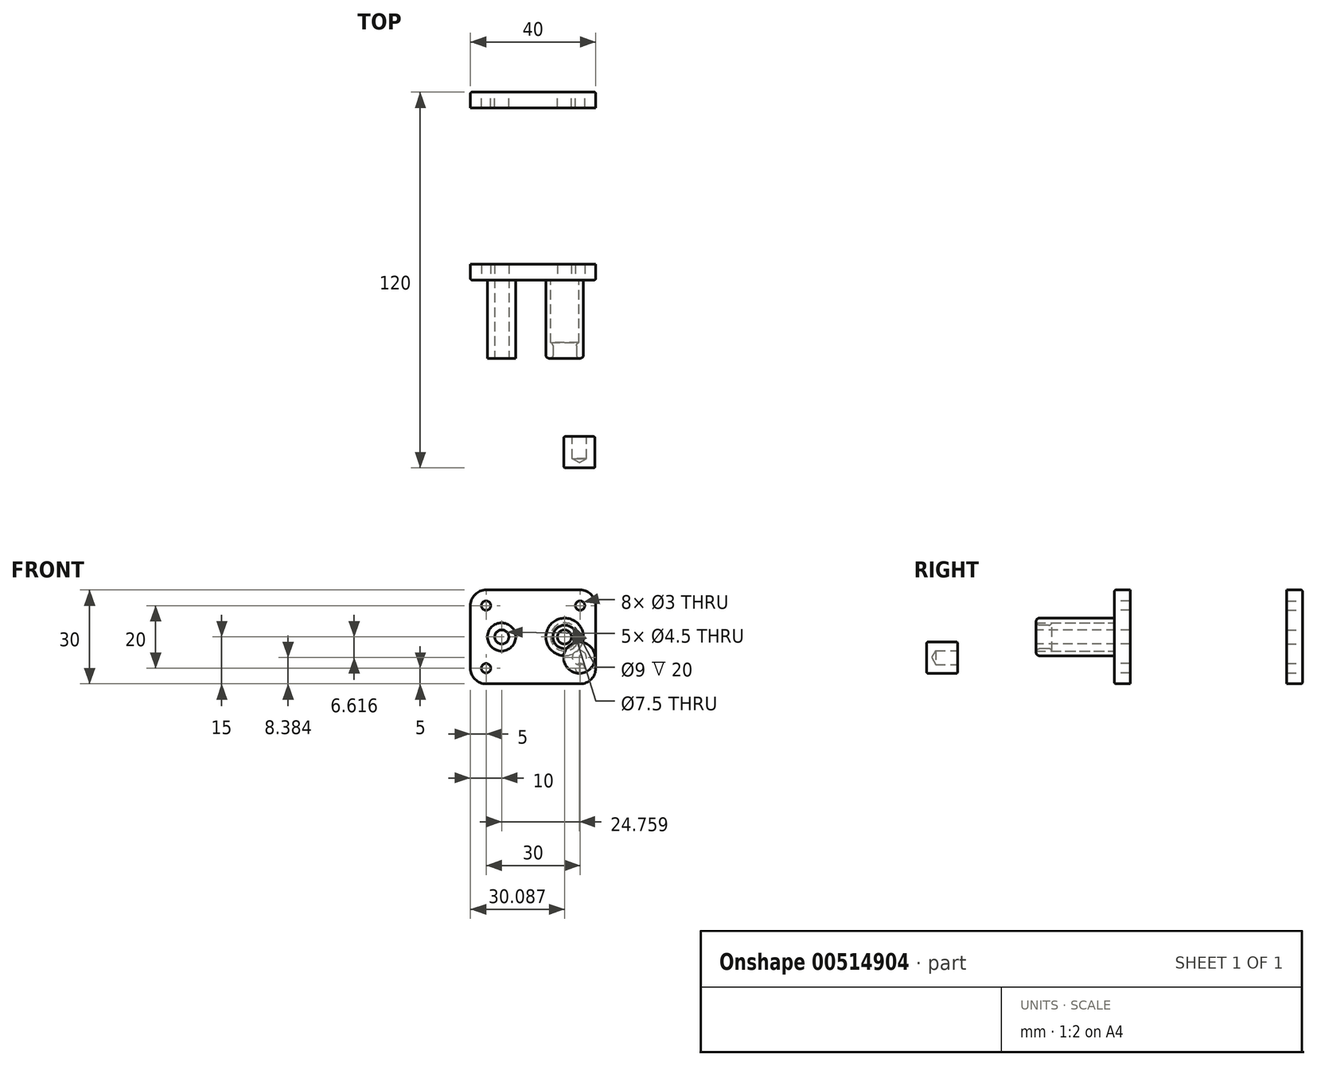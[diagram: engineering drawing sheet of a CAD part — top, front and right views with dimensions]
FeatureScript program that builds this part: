
annotation { "Feature Type Name" : "Feature", "Feature Type Description" : "" }
export const myFeature = defineFeature(function(context is Context, id is Id, definition is map)
    precondition{}
    {
        {
            var Q0;
            Q0=qCreatedBy(makeId("Front.planeOp"),FACE);
            var sketch = newSketch(context, id + "F0", { "sketchPlane" : qUnion([Q0])});
            skLineSegment(sketch, "E0.bottom", {"start": v(-15, 15) * mm, "end": v(15, 15) * mm});
            skLineSegment(sketch, "E0.top", {"start": v(-15, -15) * mm, "end": v(15, -15) * mm});
            skLineSegment(sketch, "E0.left", {"start": v(-20, 10) * mm, "end": v(-20, -10) * mm});
            skLineSegment(sketch, "E0.right", {"start": v(20, 10) * mm, "end": v(20, -10) * mm});
            skPoint(sketch, "E1", {"position": v(-10, 0) * mm});
            skPoint(sketch, "E2", {"position": v(-15, 10) * mm});
            skPoint(sketch, "E3.MirrorP", {"position": v(10, 0) * mm});
            skPoint(sketch, "E4.MirrorP", {"position": v(15, 10) * mm});
            skPoint(sketch, "E5.MirrorP", {"position": v(15, -10) * mm});
            skPoint(sketch, "E6.MirrorP", {"position": v(-15, -10) * mm});
            skPoint(sketch, "E7.visualSharp", {"position": v(-20, 15) * mm});
            skArc(sketch, "E7.filletArc", {"start": v(-15, 15) * mm, "mid": v(-18.54, 13.54) * mm, "end": v(-20, 10) * mm});
            skPoint(sketch, "E8.visualSharp", {"position": v(-20, -15) * mm});
            skArc(sketch, "E8.filletArc", {"start": v(-20, -10) * mm, "mid": v(-18.54, -13.54) * mm, "end": v(-15, -15) * mm});
            skPoint(sketch, "E9.visualSharp", {"position": v(20, -15) * mm});
            skArc(sketch, "E9.filletArc", {"start": v(15, -15) * mm, "mid": v(18.54, -13.54) * mm, "end": v(20, -10) * mm});
            skPoint(sketch, "E10.visualSharp", {"position": v(20, 15) * mm});
            skArc(sketch, "E10.filletArc", {"start": v(20, 10) * mm, "mid": v(18.54, 13.54) * mm, "end": v(15, 15) * mm});
            skSolve(sketch);
        }
        {
            var Q0;
            Q0=makeQuery(id+"F0.imprint","IMPRINT",FACE,{"disambiguationData":[TD([[makeQuery(id+"F0.imprint","IMPRINT",EDGE,{"derivedFrom":sQuery(id+"F0.wireOp",EDGE,"E0.bottom")}),-1.0]])]});
            extrude(context, id + "F1", {"entities" : qUnion([Q0]), "oppositeDirection" : true, "depth" : 5 * mm, "offsetDistance" : 25 * mm});
        }
        {
            var Q0;
            Q0=sQuery(id+"F0.wireOp",VERTEX,"E1");
            var Q1;
            Q1=sQuery(id+"F0.wireOp",VERTEX,"E3.MirrorP");
            var Q2;
            Q2=makeQuery(id+"F1.opExtrude","SWEPT_BODY",BODY,{"disambiguationData":[OSD([sQuery(id+"F0.wireOp",EDGE,"E0.bottom"),sQuery(id+"F0.wireOp",EDGE,"E0.top"),sQuery(id+"F0.wireOp",EDGE,"E0.left"),sQuery(id+"F0.wireOp",EDGE,"E0.right")])]});
            hole(context, id + "F2", {"style" : HoleStyle.SIMPLE, "endStyle" : HoleEndStyle.THROUGH, "standardTappedOrClearance" : lookupTablePath({ "standard" : "ISO", "engagement" : "50%", "pitch" : "0.8 mm", "size" : "M5", "type" : "Tapped" }), "standardBlindInLast" : lookupTablePath({ "standard" : "ISO", "engagement" : "50%", "pitch" : "0.8 mm", "size" : "M5", "type" : "Tapped" }), "holeDiameter" : 4.5 * mm, "showTappedDepth" : true, "isTappedThrough" : true, "tappedDepth" : 12 * mm, "tapClearance" : 3, "locations" : qUnion([Q0, Q1]), "scope" : qUnion([Q2]), "majorDiameter" : 5 * mm});
        }
        {
            var Q0;
            Q0=sQuery(id+"F0.wireOp",VERTEX,"E2");
            var Q1;
            Q1=sQuery(id+"F0.wireOp",VERTEX,"E4.MirrorP");
            var Q2;
            Q2=sQuery(id+"F0.wireOp",VERTEX,"E5.MirrorP");
            var Q3;
            Q3=sQuery(id+"F0.wireOp",VERTEX,"E6.MirrorP");
            var Q4;
            Q4=makeQuery(id+"F1.opExtrude","SWEPT_BODY",BODY,{"disambiguationData":[OSD([sQuery(id+"F0.wireOp",EDGE,"E0.bottom"),sQuery(id+"F0.wireOp",EDGE,"E0.top"),sQuery(id+"F0.wireOp",EDGE,"E0.left"),sQuery(id+"F0.wireOp",EDGE,"E0.right")])]});
            hole(context, id + "F3", {"style" : HoleStyle.SIMPLE, "endStyle" : HoleEndStyle.THROUGH, "standardTappedOrClearance" : lookupTablePath({ "standard" : "ISO", "size" : "3", "type" : "Drilled" }), "standardBlindInLast" : lookupTablePath({ "standard" : "ISO", "size" : "3", "type" : "Drilled" }), "holeDiameter" : 3 * mm, "isTappedThrough" : true, "tappedDepth" : 12 * mm, "tapClearance" : 3, "locations" : qUnion([Q0, Q1, Q2, Q3]), "scope" : qUnion([Q4])});
        }
        {
            var Q0;
            Q0=makeQuery(id+"F1.opExtrude","CAP_EDGE",EDGE,{"disambiguationData":[OSD([sQuery(id+"F0.wireOp",EDGE,"E0.bottom")])],"isStart":true});
            var Q1;
            Q1=makeQuery(id+"F1.opExtrude","CAP_EDGE",EDGE,{"disambiguationData":[OSD([sQuery(id+"F0.wireOp",EDGE,"E7.filletArc")])],"isStart":true});
            var Q2;
            Q2=makeQuery(id+"F3.hole-0.boolean.opBoolean","COPY",EDGE,{"derivedFrom":makeQuery(id+"F3.hole-0.opRevolve","SWEPT_EDGE",EDGE,{"disambiguationData":[OSD([sQuery(id+"F3.hole-0.sketch.wireOp",EDGE,"core_line_2"),sQuery(id+"F3.hole-0.sketch.wireOp",EDGE,"core_line_3")])]})});
            var Q3;
            Q3=makeQuery(id+"F3.hole-1.boolean.opBoolean","COPY",EDGE,{"derivedFrom":makeQuery(id+"F3.hole-1.opRevolve","SWEPT_EDGE",EDGE,{"disambiguationData":[OSD([sQuery(id+"F3.hole-1.sketch.wireOp",EDGE,"core_line_2"),sQuery(id+"F3.hole-1.sketch.wireOp",EDGE,"core_line_3")])]})});
            var Q4;
            Q4=makeQuery(id+"F3.hole-2.boolean.opBoolean","COPY",EDGE,{"derivedFrom":makeQuery(id+"F3.hole-2.opRevolve","SWEPT_EDGE",EDGE,{"disambiguationData":[OSD([sQuery(id+"F3.hole-2.sketch.wireOp",EDGE,"core_line_2"),sQuery(id+"F3.hole-2.sketch.wireOp",EDGE,"core_line_3")])]})});
            var Q5;
            Q5=makeQuery(id+"F3.hole-3.boolean.opBoolean","COPY",EDGE,{"derivedFrom":makeQuery(id+"F3.hole-3.opRevolve","SWEPT_EDGE",EDGE,{"disambiguationData":[OSD([sQuery(id+"F3.hole-3.sketch.wireOp",EDGE,"core_line_2"),sQuery(id+"F3.hole-3.sketch.wireOp",EDGE,"core_line_3")])]})});
            var Q6;
            Q6=makeQuery(id+"F2.hole-0.boolean.opBoolean","COPY",EDGE,{"derivedFrom":makeQuery(id+"F2.hole-0.opRevolve","SWEPT_EDGE",EDGE,{"disambiguationData":[OSD([sQuery(id+"F2.hole-0.sketch.wireOp",EDGE,"core_line_2"),sQuery(id+"F2.hole-0.sketch.wireOp",EDGE,"core_line_3")])]})});
            var Q7;
            Q7=makeQuery(id+"F2.hole-1.boolean.opBoolean","COPY",EDGE,{"derivedFrom":makeQuery(id+"F2.hole-1.opRevolve","SWEPT_EDGE",EDGE,{"disambiguationData":[OSD([sQuery(id+"F2.hole-1.sketch.wireOp",EDGE,"core_line_2"),sQuery(id+"F2.hole-1.sketch.wireOp",EDGE,"core_line_3")])]})});
            fillet(context, id + "F4", {"entities" : qUnion([Q0, Q1, Q2, Q3, Q4, Q5, Q6, Q7]), "radius" : 0.5 * mm, "tangentPropagation" : true, "allowEdgeOverflow" : false});
        }
        {
            var Q0;
            Q0=makeQuery(id+"F1.opExtrude","CAP_FACE",FACE,{"disambiguationData":[OSD([sQuery(id+"F0.wireOp",EDGE,"E0.bottom"),sQuery(id+"F0.wireOp",EDGE,"E0.top"),sQuery(id+"F0.wireOp",EDGE,"E0.left"),sQuery(id+"F0.wireOp",EDGE,"E0.right"),sQuery(id+"F0.wireOp",EDGE,"E7.filletArc"),sQuery(id+"F0.wireOp",EDGE,"E8.filletArc"),sQuery(id+"F0.wireOp",EDGE,"E9.filletArc"),sQuery(id+"F0.wireOp",EDGE,"E10.filletArc")])],"isStart":false});
            cPlane(context, id + "F5", {"entities" : qUnion([Q0]), "cplaneType" : CPlaneType.OFFSET, "offset" : 25 * mm, "width" : 150 * mm, "height" : 150 * mm});
        }
        {
            var Q0;
            Q0=makeQuery(id+"F1.opExtrude","SWEPT_BODY",BODY,{"disambiguationData":[OSD([sQuery(id+"F0.wireOp",EDGE,"E0.bottom"),sQuery(id+"F0.wireOp",EDGE,"E0.top"),sQuery(id+"F0.wireOp",EDGE,"E0.left"),sQuery(id+"F0.wireOp",EDGE,"E0.right"),sQuery(id+"F0.wireOp",EDGE,"E7.filletArc"),sQuery(id+"F0.wireOp",EDGE,"E8.filletArc"),sQuery(id+"F0.wireOp",EDGE,"E9.filletArc"),sQuery(id+"F0.wireOp",EDGE,"E10.filletArc")])]});
            var Q1;
            Q1=qCreatedBy(id+"F5.planeOp",FACE);
            mirror(context, id + "F6", {"entities" : qUnion([Q0]), "mirrorPlane" : qUnion([Q1])});
        }
        {
            var Q0;
            Q0=makeQuery(id+"F1.opExtrude","CAP_FACE",FACE,{"disambiguationData":[OSD([sQuery(id+"F0.wireOp",EDGE,"E0.bottom"),sQuery(id+"F0.wireOp",EDGE,"E0.top"),sQuery(id+"F0.wireOp",EDGE,"E0.left"),sQuery(id+"F0.wireOp",EDGE,"E0.right"),sQuery(id+"F0.wireOp",EDGE,"E7.filletArc"),sQuery(id+"F0.wireOp",EDGE,"E8.filletArc"),sQuery(id+"F0.wireOp",EDGE,"E9.filletArc"),sQuery(id+"F0.wireOp",EDGE,"E10.filletArc")])],"isStart":true});
            var sketch = newSketch(context, id + "F7", { "sketchPlane" : qUnion([Q0])});
            skCircle(sketch, "E11", {"center": v(10.09, 0) * mm, "radius": 4.5 * mm});
            skCircle(sketch, "E12", {"center": v(10.09, 0) * mm, "radius": 6 * mm});
            skCircle(sketch, "E13.MirrorC", {"center": v(-10.09, 0) * mm, "radius": 4.5 * mm});
            skCircle(sketch, "E14.MirrorC", {"center": v(-10.09, 0) * mm, "radius": 6 * mm});
            skSolve(sketch);
        }
        {
            var Q0;
            Q0=makeQuery(id+"F7.imprint","IMPRINT",FACE,{"disambiguationData":[TD([[makeQuery(id+"F7.imprint","IMPRINT",EDGE,{"derivedFrom":sQuery(id+"F7.wireOp",EDGE,"E11")}),-1.0]])]});
            var Q1;
            Q1=makeQuery(id+"F7.imprint","IMPRINT",FACE,{"disambiguationData":[TD([[makeQuery(id+"F7.imprint","IMPRINT",EDGE,{"derivedFrom":sQuery(id+"F7.wireOp",EDGE,"E13.MirrorC")}),1.0]])]});
            extrude(context, id + "F8", {"entities" : qUnion([Q0, Q1]), "operationType" : NewBodyOperationType.ADD, "depth" : 25 * mm, "offsetDistance" : 25 * mm});
        }
        {
            var Q0;
            Q0=makeQuery(id+"F8.opExtrude","CAP_FACE",FACE,{"disambiguationData":[OSD([sQuery(id+"F7.wireOp",EDGE,"E11"),sQuery(id+"F7.wireOp",EDGE,"E12")])],"isStart":false});
            var sketch = newSketch(context, id + "F9", { "sketchPlane" : qUnion([Q0])});
            skCircle(sketch, "E15", {"center": v(10.09, 0) * mm, "radius": 3.75 * mm});
            skCircle(sketch, "E16", {"center": v(10.09, 0) * mm, "radius": 6 * mm});
            skCircle(sketch, "E17.MirrorC", {"center": v(-10.09, 0) * mm, "radius": 6 * mm});
            skCircle(sketch, "E18.MirrorC", {"center": v(-10.09, 0) * mm, "radius": 3.75 * mm});
            skSolve(sketch);
        }
        {
            var Q0;
            Q0=makeQuery(id+"F9.imprint","IMPRINT",FACE,{"disambiguationData":[TD([[makeQuery(id+"F9.imprint","IMPRINT",EDGE,{"derivedFrom":sQuery(id+"F9.wireOp",EDGE,"E15")}),-1.0]])]});
            var Q1;
            Q1=makeQuery(id+"F9.imprint","IMPRINT",FACE,{"disambiguationData":[TD([[makeQuery(id+"F9.imprint","IMPRINT",EDGE,{"derivedFrom":sQuery(id+"F9.wireOp",EDGE,"E16")}),1.0]])]});
            var Q2;
            Q2=makeQuery(id+"F9.imprint","IMPRINT",FACE,{"disambiguationData":[TD([[makeQuery(id+"F9.imprint","IMPRINT",EDGE,{"derivedFrom":sQuery(id+"F9.wireOp",EDGE,"E17.MirrorC")}),-1.0]])]});
            extrude(context, id + "F10", {"entities" : qUnion([Q0, Q1, Q2]), "operationType" : NewBodyOperationType.ADD, "oppositeDirection" : true, "depth" : 5 * mm, "offsetDistance" : 25 * mm});
        }
        {
            var Q0;
            Q0=makeQuery(id+"F8.opExtrude","CAP_EDGE",EDGE,{"disambiguationData":[OSD([sQuery(id+"F7.wireOp",EDGE,"E12")])],"isStart":true});
            var Q1;
            Q1=makeQuery(id+"F8.opExtrude","CAP_EDGE",EDGE,{"disambiguationData":[OSD([sQuery(id+"F7.wireOp",EDGE,"E14.MirrorC")])],"isStart":true});
            var Q2;
            Q2=makeQuery(id+"F8.opExtrude","CAP_EDGE",EDGE,{"disambiguationData":[OSD([sQuery(id+"F7.wireOp",EDGE,"E14.MirrorC")])],"isStart":false});
            var Q3;
            Q3=makeQuery(id+"F10.opExtrude","CAP_EDGE",EDGE,{"disambiguationData":[OSD([sQuery(id+"F9.wireOp",EDGE,"E18.MirrorC")])],"isStart":false});
            var Q4;
            Q4=makeQuery(id+"F10.opExtrude","CAP_EDGE",EDGE,{"disambiguationData":[OSD([sQuery(id+"F9.wireOp",EDGE,"E18.MirrorC")])],"isStart":true});
            var Q5;
            Q5=makeQuery(id+"F10.opExtrude","CAP_EDGE",EDGE,{"disambiguationData":[OSD([sQuery(id+"F9.wireOp",EDGE,"E15")])],"isStart":false});
            var Q6;
            Q6=makeQuery(id+"F10.opExtrude","CAP_EDGE",EDGE,{"disambiguationData":[OSD([sQuery(id+"F9.wireOp",EDGE,"E15")])],"isStart":true});
            var Q7;
            Q7=makeQuery(id+"F8.opExtrude","CAP_EDGE",EDGE,{"disambiguationData":[OSD([sQuery(id+"F7.wireOp",EDGE,"E12")])],"isStart":false});
            fillet(context, id + "F11", {"entities" : qUnion([Q0, Q1, Q2, Q3, Q4, Q5, Q6, Q7]), "radius" : 1 * mm, "tangentPropagation" : true, "allowEdgeOverflow" : false});
        }
        {
            var Q0;
            {var subQ0=sQuery(id+"F0.wireOp",EDGE,"E10.filletArc");var subQ1=sQuery(id+"F0.wireOp",EDGE,"E9.filletArc");var subQ2=sQuery(id+"F0.wireOp",EDGE,"E8.filletArc");var subQ3=sQuery(id+"F0.wireOp",EDGE,"E7.filletArc");var subQ4=sQuery(id+"F0.wireOp",EDGE,"E0.bottom");var subQ5=sQuery(id+"F0.wireOp",EDGE,"E0.top");var subQ6=sQuery(id+"F0.wireOp",EDGE,"E0.left");var subQ7=sQuery(id+"F0.wireOp",EDGE,"E0.right");Q0=makeQuery(id+"F8.boolean.opBoolean","SPLIT",FACE,{"disambiguationData":[TD([makeQuery(id+"F4.opFillet","BLEND_FACE",FACE,{"disambiguationData":[OSD([subQ4])]})])],"derivedFrom":makeQuery(id+"F1.opExtrude","CAP_FACE",FACE,{"disambiguationData":[OSD([subQ4,subQ5,subQ6,subQ7,subQ3,subQ2,subQ1,subQ0])],"isStart":true})});}
            cPlane(context, id + "F12", {"entities" : qUnion([Q0]), "cplaneType" : CPlaneType.OFFSET, "offset" : 50 * mm, "width" : 150 * mm, "height" : 150 * mm});
        }
        {
            var Q0;
            Q0=qCreatedBy(id+"F12.planeOp",FACE);
            var sketch = newSketch(context, id + "F13", { "sketchPlane" : qUnion([Q0])});
            skCircle(sketch, "E19", {"center": v(14.76, -6.62) * mm, "radius": 5 * mm});
            skSolve(sketch);
        }
        {
            var Q0;
            Q0=makeQuery(id+"F13.imprint","IMPRINT",FACE,{"disambiguationData":[TD([[makeQuery(id+"F13.imprint","IMPRINT",EDGE,{"derivedFrom":sQuery(id+"F13.wireOp",EDGE,"E19")}),1.0]])]});
            extrude(context, id + "F14", {"entities" : qUnion([Q0]), "depth" : 10 * mm, "offsetDistance" : 25 * mm});
        }
        {
            var Q0;
            Q0=sQuery(id+"F13.wireOp",VERTEX,"E19.center");
            var Q1;
            Q1=makeQuery(id+"F14.opExtrude","SWEPT_BODY",BODY,{"disambiguationData":[OSD([sQuery(id+"F13.wireOp",EDGE,"E19")])]});
            hole(context, id + "F15", {"style" : HoleStyle.SIMPLE, "endStyle" : HoleEndStyle.BLIND, "oppositeDirection" : true, "standardTappedOrClearance" : lookupTablePath({ "standard" : "ISO", "engagement" : "50%", "pitch" : "0.8 mm", "size" : "M5", "type" : "Tapped" }), "standardBlindInLast" : lookupTablePath({ "standard" : "ISO", "engagement" : "50%", "pitch" : "0.8 mm", "size" : "M5", "type" : "Tapped" }), "holeDiameter" : 4.5 * mm, "showTappedDepth" : true, "holeDepth" : 7 * mm, "isTappedThrough" : true, "tappedDepth" : 4.6 * mm, "tapClearance" : 3, "locations" : qUnion([Q0]), "scope" : qUnion([Q1]), "majorDiameter" : 5 * mm});
        }
        {
            var Q0;
            Q0=makeQuery(id+"F14.opExtrude","CAP_EDGE",EDGE,{"disambiguationData":[OSD([sQuery(id+"F13.wireOp",EDGE,"E19")])],"isStart":false});
            var Q1;
            Q1=makeQuery(id+"F14.opExtrude","CAP_EDGE",EDGE,{"disambiguationData":[OSD([sQuery(id+"F13.wireOp",EDGE,"E19")])],"isStart":true});
            fillet(context, id + "F16", {"entities" : qUnion([Q0, Q1]), "radius" : 0.5 * mm, "tangentPropagation" : true, "allowEdgeOverflow" : false});
        }
    });
